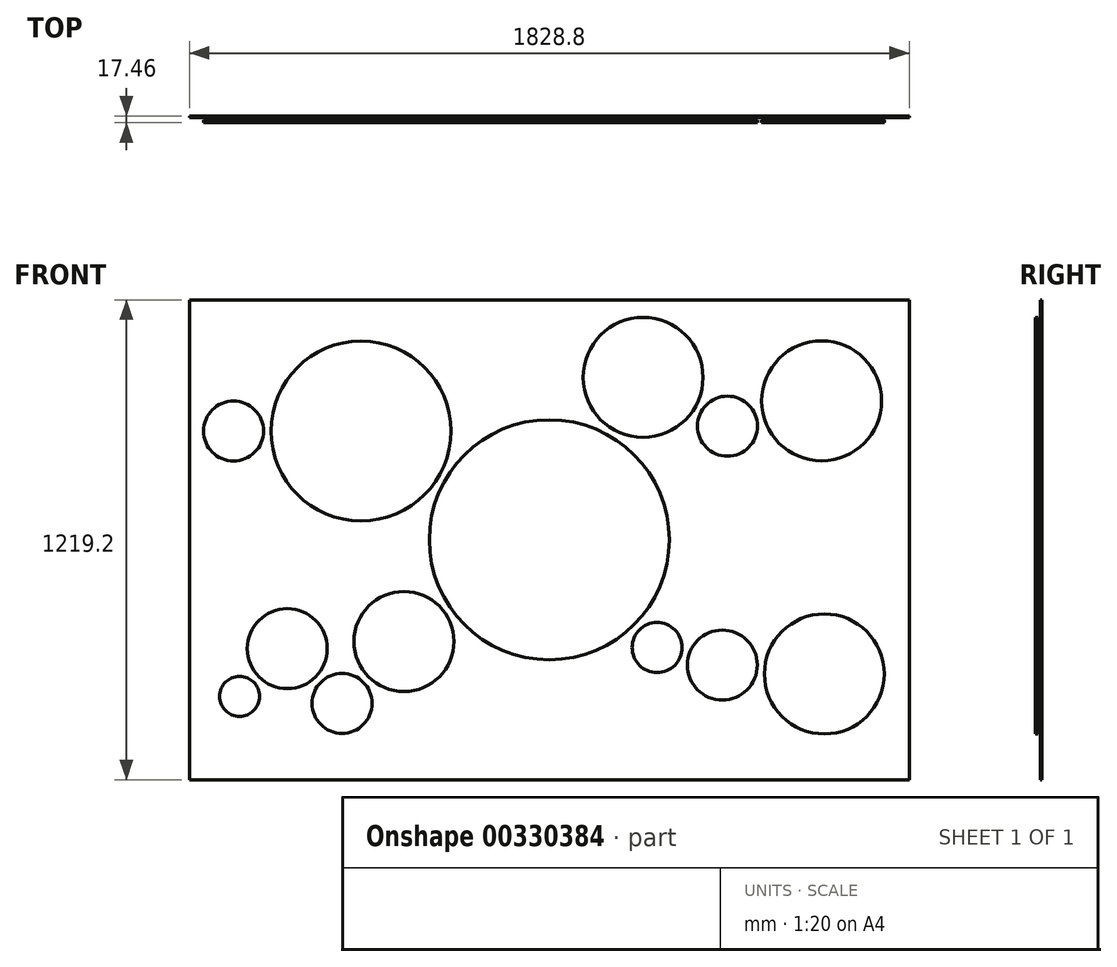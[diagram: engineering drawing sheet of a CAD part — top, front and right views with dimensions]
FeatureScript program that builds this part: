
annotation { "Feature Type Name" : "Feature", "Feature Type Description" : "" }
export const myFeature = defineFeature(function(context is Context, id is Id, definition is map)
    precondition{}
    {
        {
            var Q0;
            Q0=qCreatedBy(makeId("Front.planeOp"),FACE);
            var sketch = newSketch(context, id + "F0", { "sketchPlane" : qUnion([Q0])});
            skLineSegment(sketch, "E0", {"start": v(0, 0) * mm, "end": v(-914.4, 0) * mm});
            skLineSegment(sketch, "E1", {"start": v(-914.4, 0) * mm, "end": v(-914.4, 1219.2) * mm});
            skLineSegment(sketch, "E2", {"start": v(-914.4, 1219.2) * mm, "end": v(914.4, 1219.2) * mm});
            skLineSegment(sketch, "E3", {"start": v(914.4, 1219.2) * mm, "end": v(914.4, 0) * mm});
            skLineSegment(sketch, "E4", {"start": v(914.4, 0) * mm, "end": v(0, 0) * mm});
            skLineSegment(sketch, "E5", {"start": v(0, 0) * mm, "end": v(0, 1219.2) * mm, "construction": true});
            skSolve(sketch);
        }
        {
            var Q0;
            Q0=makeQuery(id+"F0.imprint","IMPRINT",FACE,{"disambiguationData":[TD([[makeQuery(id+"F0.imprint","IMPRINT",EDGE,{"derivedFrom":sQuery(id+"F0.wireOp",EDGE,"E0")}),-1.0]])]});
            extrude(context, id + "F1", {"entities" : qUnion([Q0]), "depth" : 4.76 * mm});
        }
        {
            var Q0;
            Q0=makeQuery(id+"F1.opExtrude","CAP_FACE",FACE,{"disambiguationData":[OSD([sQuery(id+"F0.wireOp",EDGE,"E0"),sQuery(id+"F0.wireOp",EDGE,"E1"),sQuery(id+"F0.wireOp",EDGE,"E2"),sQuery(id+"F0.wireOp",EDGE,"E3"),sQuery(id+"F0.wireOp",EDGE,"E4")])],"isStart":false});
            cPlane(context, id + "F2", {"entities" : qUnion([Q0]), "cplaneType" : CPlaneType.OFFSET, "offset" : 6.35 * mm, "width" : 152.4 * mm, "height" : 152.4 * mm});
        }
        {
            var Q0;
            Q0=qCreatedBy(id+"F2.planeOp",FACE);
            var sketch = newSketch(context, id + "F3", { "sketchPlane" : qUnion([Q0])});
            skLineSegment(sketch, "E6", {"start": v(0, 0) * mm, "end": v(0, 1219.2) * mm, "construction": true});
            skLineSegment(sketch, "E7", {"start": v(0, 609.6) * mm, "end": v(-914.4, 609.6) * mm, "construction": true});
            skLineSegment(sketch, "E8", {"start": v(0, 609.6) * mm, "end": v(914.4, 609.6) * mm, "construction": true});
            skCircle(sketch, "E9", {"center": v(0, 609.6) * mm, "radius": 304.8 * mm});
            skCircle(sketch, "E10", {"center": v(-369.31, 351) * mm, "radius": 127 * mm});
            skCircle(sketch, "E11", {"center": v(-526.47, 193.85) * mm, "radius": 76.2 * mm});
            skCircle(sketch, "E12", {"center": v(-665.66, 333.04) * mm, "radius": 101.6 * mm});
            skCircle(sketch, "E13", {"center": v(-786.9, 211.8) * mm, "radius": 50.8 * mm});
            skCircle(sketch, "E14", {"center": v(-802.29, 885.82) * mm, "radius": 76.2 * mm});
            skCircle(sketch, "E15", {"center": v(-478.44, 885.82) * mm, "radius": 228.6 * mm});
            skCircle(sketch, "E16", {"center": v(273.9, 335.7) * mm, "radius": 63.5 * mm});
            skCircle(sketch, "E17", {"center": v(439.5, 291.33) * mm, "radius": 88.9 * mm});
            skCircle(sketch, "E18", {"center": v(698.87, 268.64) * mm, "radius": 152.4 * mm});
            skCircle(sketch, "E19", {"center": v(238.13, 1022.04) * mm, "radius": 152.4 * mm});
            skCircle(sketch, "E20", {"center": v(452.6, 898.22) * mm, "radius": 76.2 * mm});
            skCircle(sketch, "E21", {"center": v(691.8, 962.32) * mm, "radius": 152.4 * mm});
            skLineSegment(sketch, "E22", {"start": v(0, 609.6) * mm, "end": v(-478.44, 885.82) * mm, "construction": true});
            skLineSegment(sketch, "E23", {"start": v(-478.44, 885.82) * mm, "end": v(-802.29, 885.82) * mm, "construction": true});
            skLineSegment(sketch, "E24", {"start": v(0, 609.6) * mm, "end": v(-369.31, 351) * mm, "construction": true});
            skLineSegment(sketch, "E25", {"start": v(-369.31, 351) * mm, "end": v(-526.47, 193.85) * mm, "construction": true});
            skLineSegment(sketch, "E26", {"start": v(-526.47, 193.85) * mm, "end": v(-665.66, 333.04) * mm, "construction": true});
            skLineSegment(sketch, "E27", {"start": v(-665.66, 333.04) * mm, "end": v(-786.9, 211.8) * mm, "construction": true});
            skLineSegment(sketch, "E28", {"start": v(0, 609.6) * mm, "end": v(273.9, 335.7) * mm, "construction": true});
            skLineSegment(sketch, "E29", {"start": v(273.9, 335.7) * mm, "end": v(439.5, 291.33) * mm, "construction": true});
            skLineSegment(sketch, "E30", {"start": v(439.5, 291.33) * mm, "end": v(698.87, 268.64) * mm, "construction": true});
            skLineSegment(sketch, "E31", {"start": v(238.13, 1022.04) * mm, "end": v(452.6, 898.22) * mm, "construction": true});
            skLineSegment(sketch, "E32", {"start": v(452.6, 898.22) * mm, "end": v(691.8, 962.32) * mm, "construction": true});
            skLineSegment(sketch, "E33", {"start": v(238.13, 1022.04) * mm, "end": v(0, 609.6) * mm, "construction": true});
            skSolve(sketch);
        }
        {
            var Q0;
            Q0 = qSketchRegion(id + "F3", true);
            extrude(context, id + "F4", {"entities" : qUnion([Q0]), "depth" : 6.35 * mm});
        }
    });
